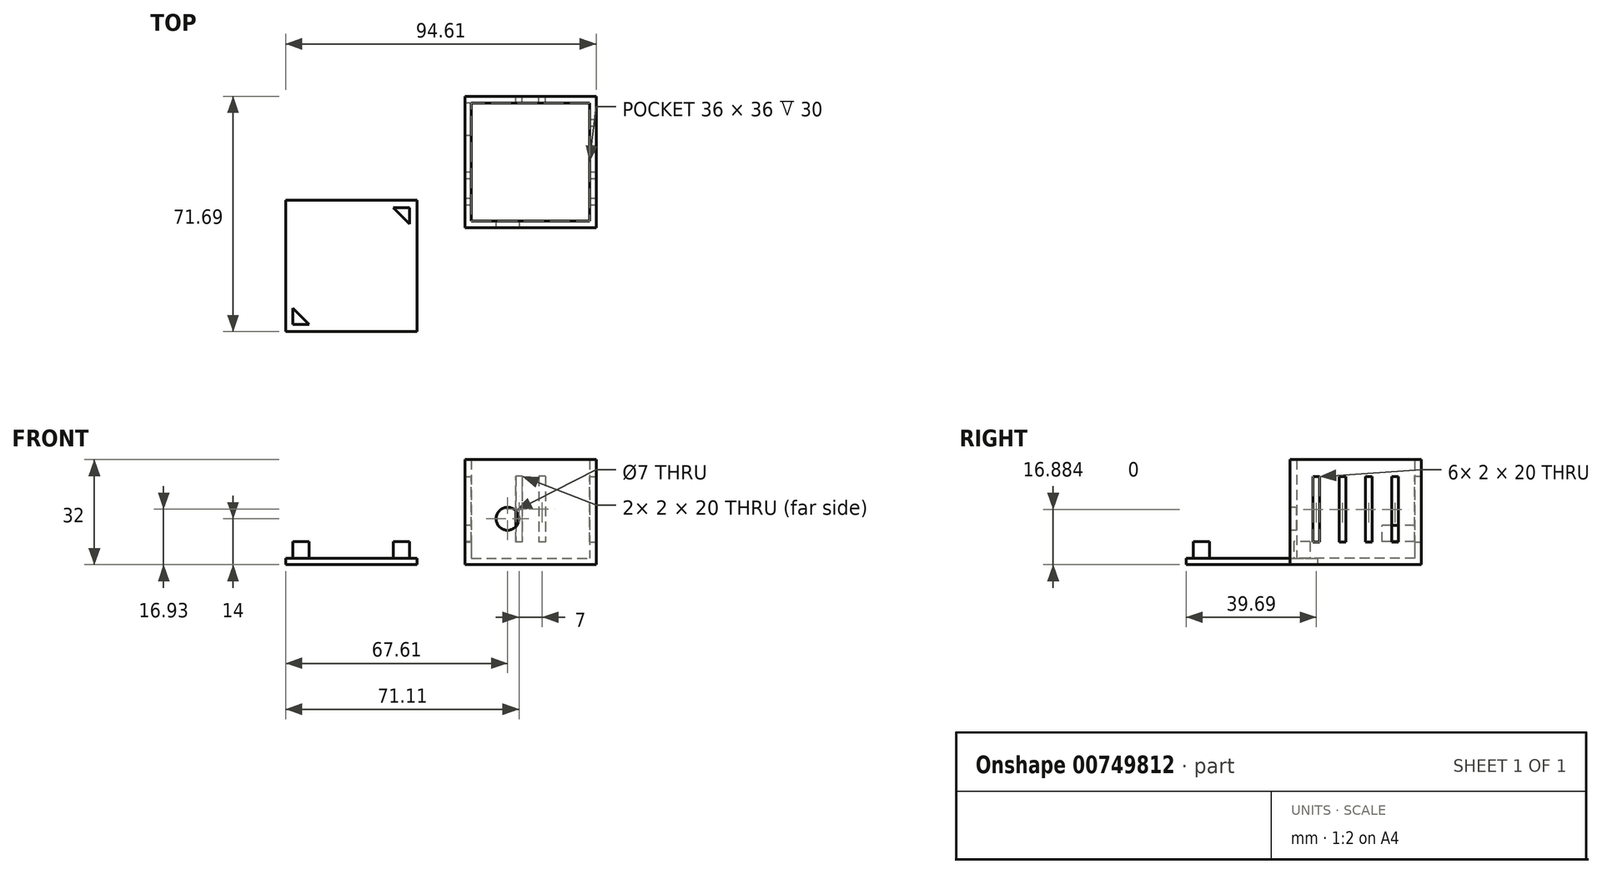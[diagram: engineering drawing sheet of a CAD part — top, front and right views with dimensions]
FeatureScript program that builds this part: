
annotation { "Feature Type Name" : "Feature", "Feature Type Description" : "" }
export const myFeature = defineFeature(function(context is Context, id is Id, definition is map)
    precondition{}
    {
        {
            var Q0;
            Q0=qCreatedBy(makeId("Top.planeOp"),FACE);
            var sketch = newSketch(context, id + "F0", { "sketchPlane" : qUnion([Q0])});
            skLineSegment(sketch, "E0.bottom", {"start": v(18, -18) * mm, "end": v(-18, -18) * mm});
            skLineSegment(sketch, "E0.top", {"start": v(18, 18) * mm, "end": v(-18, 18) * mm});
            skLineSegment(sketch, "E0.left", {"start": v(18, -18) * mm, "end": v(18, 18) * mm});
            skLineSegment(sketch, "E0.right", {"start": v(-18, -18) * mm, "end": v(-18, 18) * mm});
            skPoint(sketch, "E0.middle", {"position": v(0, 0) * mm});
            skLineSegment(sketch, "E1.bottom", {"start": v(20, -20) * mm, "end": v(-20, -20) * mm});
            skLineSegment(sketch, "E1.top", {"start": v(20, 20) * mm, "end": v(-20, 20) * mm});
            skLineSegment(sketch, "E1.left", {"start": v(20, -20) * mm, "end": v(20, 20) * mm});
            skLineSegment(sketch, "E1.right", {"start": v(-20, -20) * mm, "end": v(-20, 20) * mm});
            skSolve(sketch);
        }
        {
            var Q0;
            Q0=makeQuery(id+"F0.imprint","IMPRINT",FACE,{"disambiguationData":[TD([[makeQuery(id+"F0.imprint","IMPRINT",EDGE,{"derivedFrom":sQuery(id+"F0.wireOp",EDGE,"E0.bottom")}),-1.0]])]});
            var Q1;
            Q1=makeQuery(id+"F0.imprint","IMPRINT",FACE,{"disambiguationData":[TD([[makeQuery(id+"F0.imprint","IMPRINT",EDGE,{"derivedFrom":sQuery(id+"F0.wireOp",EDGE,"E0.bottom")}),1.0]])]});
            extrude(context, id + "F1", {"entities" : qUnion([Q0, Q1]), "depth" : 2 * mm, "offsetDistance" : 25 * mm});
        }
        {
            var Q0;
            Q0=makeQuery(id+"F0.imprint","IMPRINT",FACE,{"disambiguationData":[TD([[makeQuery(id+"F0.imprint","IMPRINT",EDGE,{"derivedFrom":sQuery(id+"F0.wireOp",EDGE,"E0.bottom")}),1.0]])]});
            extrude(context, id + "F2", {"entities" : qUnion([Q0]), "operationType" : NewBodyOperationType.ADD, "depth" : 32 * mm, "offsetDistance" : 25 * mm});
        }
        {
            var Q0;
            {var subQ0=sQuery(id+"F0.wireOp",EDGE,"E1.right");Q0=makeQuery(id+"F2.boolean.opBoolean","MERGE",FACE,{"derivedFrom":[makeQuery(id+"F1.opExtrude","SWEPT_FACE",FACE,{"disambiguationData":[OSD([subQ0])]}),makeQuery(id+"F2.opExtrude","SWEPT_FACE",FACE,{"disambiguationData":[OSD([subQ0])]})]});}
            var sketch = newSketch(context, id + "F3", { "sketchPlane" : qUnion([Q0])});
            skLineSegment(sketch, "E2.bottom", {"start": v(-18, 7) * mm, "end": v(-8, 7) * mm});
            skLineSegment(sketch, "E2.top", {"start": v(-18, 12) * mm, "end": v(-8, 12) * mm});
            skLineSegment(sketch, "E2.left", {"start": v(-18, 7) * mm, "end": v(-18, 12) * mm});
            skLineSegment(sketch, "E2.right", {"start": v(-8, 7) * mm, "end": v(-8, 12) * mm});
            skSolve(sketch);
        }
        {
            var Q0;
            Q0=makeQuery(id+"F3.imprint","IMPRINT",FACE,{"disambiguationData":[TD([[makeQuery(id+"F3.imprint","IMPRINT",EDGE,{"derivedFrom":sQuery(id+"F3.wireOp",EDGE,"E2.bottom")}),1.0]])]});
            extrude(context, id + "F4", {"entities" : qUnion([Q0]), "operationType" : NewBodyOperationType.REMOVE, "oppositeDirection" : true, "depth" : 2 * mm, "offsetDistance" : 25 * mm});
        }
        {
            var Q0;
            {var subQ0=sQuery(id+"F0.wireOp",EDGE,"E1.bottom");Q0=makeQuery(id+"F2.boolean.opBoolean","MERGE",FACE,{"derivedFrom":[makeQuery(id+"F1.opExtrude","SWEPT_FACE",FACE,{"disambiguationData":[OSD([subQ0])]}),makeQuery(id+"F2.opExtrude","SWEPT_FACE",FACE,{"disambiguationData":[OSD([subQ0])]})]});}
            var sketch = newSketch(context, id + "F5", { "sketchPlane" : qUnion([Q0])});
            skPoint(sketch, "E3", {"position": v(-7, 14) * mm});
            skSolve(sketch);
        }
        {
            var Q0;
            Q0=sQuery(id+"F5.wireOp",VERTEX,"E3");
            var Q1;
            Q1=makeQuery(id+"F1.opExtrude","SWEPT_BODY",BODY,{"disambiguationData":[OSD([sQuery(id+"F0.wireOp",EDGE,"E1.bottom"),sQuery(id+"F0.wireOp",EDGE,"E1.top"),sQuery(id+"F0.wireOp",EDGE,"E1.left"),sQuery(id+"F0.wireOp",EDGE,"E1.right")])]});
            hole(context, id + "F6", {"style" : HoleStyle.SIMPLE, "endStyle" : HoleEndStyle.BLIND, "holeDiameter" : 7 * mm, "majorDiameter" : 5 * mm, "holeDepth" : 5 * mm, "isTappedThrough" : true, "tappedDepth" : 12 * mm, "tapClearance" : 3, "locations" : qUnion([Q0]), "scope" : qUnion([Q1])});
        }
        {
            var Q0;
            {var subQ0=sQuery(id+"F0.wireOp",EDGE,"E1.left");Q0=makeQuery(id+"F2.boolean.opBoolean","MERGE",FACE,{"derivedFrom":[makeQuery(id+"F1.opExtrude","SWEPT_FACE",FACE,{"disambiguationData":[OSD([subQ0])]}),makeQuery(id+"F2.opExtrude","SWEPT_FACE",FACE,{"disambiguationData":[OSD([subQ0])]})]});}
            var sketch = newSketch(context, id + "F7", { "sketchPlane" : qUnion([Q0])});
            skLineSegment(sketch, "E4.bottom", {"start": v(-13, 26.88) * mm, "end": v(-11, 26.88) * mm});
            skLineSegment(sketch, "E4.top", {"start": v(-13, 6.88) * mm, "end": v(-11, 6.88) * mm});
            skLineSegment(sketch, "E4.left", {"start": v(-13, 26.88) * mm, "end": v(-13, 6.88) * mm});
            skLineSegment(sketch, "E4.right", {"start": v(-11, 26.88) * mm, "end": v(-11, 6.88) * mm});
            skLineSegment(sketch, "E5.bottom", {"start": v(-5, 26.88) * mm, "end": v(-3, 26.88) * mm});
            skLineSegment(sketch, "E5.top", {"start": v(-5, 6.88) * mm, "end": v(-3, 6.88) * mm});
            skLineSegment(sketch, "E5.left", {"start": v(-5, 26.88) * mm, "end": v(-5, 6.88) * mm});
            skLineSegment(sketch, "E5.right", {"start": v(-3, 26.88) * mm, "end": v(-3, 6.88) * mm});
            skPoint(sketch, "E6.firstSnap0", {"position": v(-4, 26.88) * mm});
            skLineSegment(sketch, "E6.bottom", {"start": v(3, 26.88) * mm, "end": v(5, 26.88) * mm});
            skLineSegment(sketch, "E6.top", {"start": v(3, 6.88) * mm, "end": v(5, 6.88) * mm});
            skLineSegment(sketch, "E6.left", {"start": v(3, 26.88) * mm, "end": v(3, 6.88) * mm});
            skLineSegment(sketch, "E6.right", {"start": v(5, 26.88) * mm, "end": v(5, 6.88) * mm});
            skLineSegment(sketch, "E7.bottom", {"start": v(11, 26.88) * mm, "end": v(13, 26.88) * mm});
            skLineSegment(sketch, "E7.top", {"start": v(11, 6.88) * mm, "end": v(13, 6.88) * mm});
            skLineSegment(sketch, "E7.left", {"start": v(11, 26.88) * mm, "end": v(11, 6.88) * mm});
            skLineSegment(sketch, "E7.right", {"start": v(13, 26.88) * mm, "end": v(13, 6.88) * mm});
            skSolve(sketch);
        }
        {
            var Q0;
            Q0=makeQuery(id+"F7.imprint","IMPRINT",FACE,{"disambiguationData":[TD([[makeQuery(id+"F7.imprint","IMPRINT",EDGE,{"derivedFrom":sQuery(id+"F7.wireOp",EDGE,"E4.bottom")}),-1.0]])]});
            var Q1;
            Q1=makeQuery(id+"F7.imprint","IMPRINT",FACE,{"disambiguationData":[TD([[makeQuery(id+"F7.imprint","IMPRINT",EDGE,{"derivedFrom":sQuery(id+"F7.wireOp",EDGE,"E5.bottom")}),-1.0]])]});
            extrude(context, id + "F8", {"entities" : qUnion([Q0, Q1]), "operationType" : NewBodyOperationType.REMOVE, "oppositeDirection" : true, "depth" : 40 * mm, "offsetDistance" : 25 * mm});
        }
        {
            var Q0;
            Q0=makeQuery(id+"F7.imprint","IMPRINT",FACE,{"disambiguationData":[TD([[makeQuery(id+"F7.imprint","IMPRINT",EDGE,{"derivedFrom":sQuery(id+"F7.wireOp",EDGE,"E6.bottom")}),-1.0]])]});
            var Q1;
            Q1=makeQuery(id+"F7.imprint","IMPRINT",FACE,{"disambiguationData":[TD([[makeQuery(id+"F7.imprint","IMPRINT",EDGE,{"derivedFrom":sQuery(id+"F7.wireOp",EDGE,"E7.bottom")}),-1.0]])]});
            extrude(context, id + "F9", {"entities" : qUnion([Q0, Q1]), "operationType" : NewBodyOperationType.REMOVE, "oppositeDirection" : true, "depth" : 25 * mm, "offsetDistance" : 25 * mm});
        }
        {
            var Q0;
            {var subQ0=sQuery(id+"F0.wireOp",EDGE,"E1.top");Q0=makeQuery(id+"F2.boolean.opBoolean","MERGE",FACE,{"derivedFrom":[makeQuery(id+"F1.opExtrude","SWEPT_FACE",FACE,{"disambiguationData":[OSD([subQ0])]}),makeQuery(id+"F2.opExtrude","SWEPT_FACE",FACE,{"disambiguationData":[OSD([subQ0])]})]});}
            var sketch = newSketch(context, id + "F10", { "sketchPlane" : qUnion([Q0])});
            skLineSegment(sketch, "E8.bottom", {"start": v(-4.5, 26.93) * mm, "end": v(-2.5, 26.93) * mm});
            skLineSegment(sketch, "E8.top", {"start": v(-4.5, 6.93) * mm, "end": v(-2.5, 6.93) * mm});
            skLineSegment(sketch, "E8.left", {"start": v(-4.5, 26.93) * mm, "end": v(-4.5, 6.93) * mm});
            skLineSegment(sketch, "E8.right", {"start": v(-2.5, 26.93) * mm, "end": v(-2.5, 6.93) * mm});
            skLineSegment(sketch, "E9.bottom", {"start": v(2.5, 26.93) * mm, "end": v(4.5, 26.93) * mm});
            skLineSegment(sketch, "E9.top", {"start": v(2.5, 6.93) * mm, "end": v(4.5, 6.93) * mm});
            skLineSegment(sketch, "E9.left", {"start": v(2.5, 26.93) * mm, "end": v(2.5, 6.93) * mm});
            skLineSegment(sketch, "E9.right", {"start": v(4.5, 26.93) * mm, "end": v(4.5, 6.93) * mm});
            skSolve(sketch);
        }
        {
            var Q0;
            Q0=makeQuery(id+"F10.imprint","IMPRINT",FACE,{"disambiguationData":[TD([[makeQuery(id+"F10.imprint","IMPRINT",EDGE,{"derivedFrom":sQuery(id+"F10.wireOp",EDGE,"E8.bottom")}),-1.0]])]});
            var Q1;
            Q1=makeQuery(id+"F10.imprint","IMPRINT",FACE,{"disambiguationData":[TD([[makeQuery(id+"F10.imprint","IMPRINT",EDGE,{"derivedFrom":sQuery(id+"F10.wireOp",EDGE,"E9.bottom")}),-1.0]])]});
            extrude(context, id + "F11", {"entities" : qUnion([Q0, Q1]), "operationType" : NewBodyOperationType.REMOVE, "oppositeDirection" : true, "depth" : 25 * mm, "offsetDistance" : 25 * mm});
        }
        {
            var Q0;
            Q0=qCreatedBy(makeId("Top.planeOp"),FACE);
            var sketch = newSketch(context, id + "F12", { "sketchPlane" : qUnion([Q0])});
            skLineSegment(sketch, "E10.bottom", {"start": v(-34.6, -51.69) * mm, "end": v(-74.6, -51.69) * mm});
            skLineSegment(sketch, "E10.top", {"start": v(-34.6, -11.69) * mm, "end": v(-74.6, -11.69) * mm});
            skLineSegment(sketch, "E10.left", {"start": v(-34.6, -51.69) * mm, "end": v(-34.6, -11.69) * mm});
            skLineSegment(sketch, "E10.right", {"start": v(-74.6, -51.69) * mm, "end": v(-74.6, -11.69) * mm});
            skPoint(sketch, "E10.middle", {"position": v(-54.6, -31.69) * mm});
            skLineSegment(sketch, "E11", {"start": v(-36.8, -13.89) * mm, "end": v(-41.8, -13.89) * mm});
            skLineSegment(sketch, "E12", {"start": v(-36.8, -13.89) * mm, "end": v(-36.8, -18.89) * mm});
            skLineSegment(sketch, "E13", {"start": v(-36.8, -18.89) * mm, "end": v(-41.8, -13.89) * mm});
            skLineSegment(sketch, "E14", {"start": v(-67.4, -49.49) * mm, "end": v(-72.4, -49.49) * mm});
            skLineSegment(sketch, "E15", {"start": v(-72.4, -49.49) * mm, "end": v(-72.4, -44.49) * mm});
            skLineSegment(sketch, "E16", {"start": v(-72.4, -44.49) * mm, "end": v(-67.4, -49.49) * mm});
            skSolve(sketch);
        }
        {
            var Q0;
            Q0=makeQuery(id+"F12.imprint","IMPRINT",FACE,{"disambiguationData":[TD([[makeQuery(id+"F12.imprint","IMPRINT",EDGE,{"derivedFrom":sQuery(id+"F12.wireOp",EDGE,"E10.bottom")}),-1.0]])]});
            var Q1;
            Q1=makeQuery(id+"F12.imprint","IMPRINT",FACE,{"disambiguationData":[TD([[makeQuery(id+"F12.imprint","IMPRINT",EDGE,{"derivedFrom":sQuery(id+"F12.wireOp",EDGE,"E14")}),-1.0]])]});
            var Q2;
            Q2=makeQuery(id+"F12.imprint","IMPRINT",FACE,{"disambiguationData":[TD([[makeQuery(id+"F12.imprint","IMPRINT",EDGE,{"derivedFrom":sQuery(id+"F12.wireOp",EDGE,"E11")}),1.0]])]});
            extrude(context, id + "F13", {"entities" : qUnion([Q0, Q1, Q2]), "depth" : 2 * mm, "offsetDistance" : 25 * mm});
        }
        {
            var Q0;
            Q0=makeQuery(id+"F12.imprint","IMPRINT",FACE,{"disambiguationData":[TD([[makeQuery(id+"F12.imprint","IMPRINT",EDGE,{"derivedFrom":sQuery(id+"F12.wireOp",EDGE,"E14")}),-1.0]])]});
            var Q1;
            Q1=makeQuery(id+"F12.imprint","IMPRINT",FACE,{"disambiguationData":[TD([[makeQuery(id+"F12.imprint","IMPRINT",EDGE,{"derivedFrom":sQuery(id+"F12.wireOp",EDGE,"E11")}),1.0]])]});
            extrude(context, id + "F14", {"entities" : qUnion([Q0, Q1]), "operationType" : NewBodyOperationType.ADD, "depth" : 7 * mm, "offsetDistance" : 25 * mm});
        }
    });
